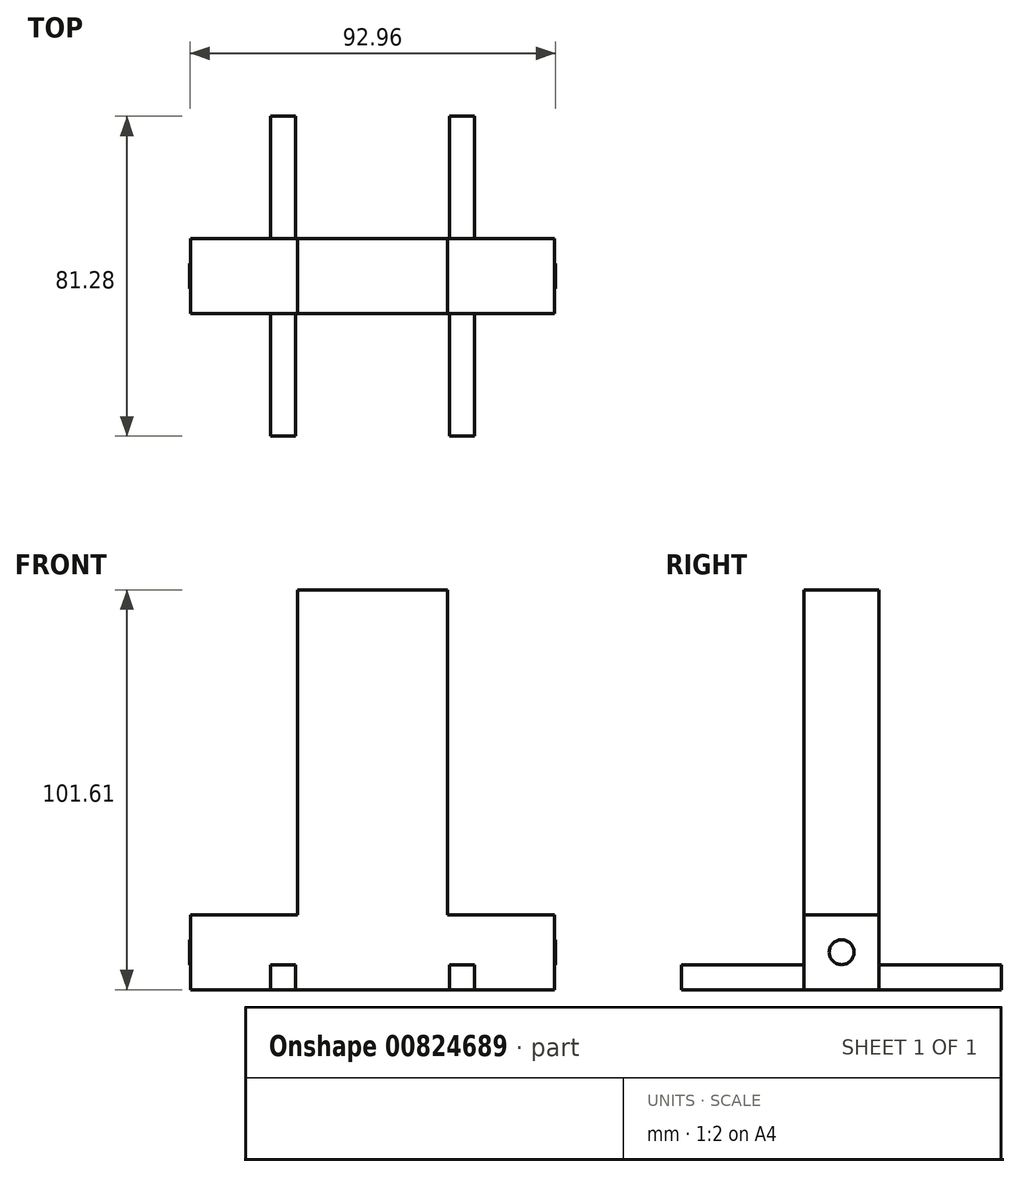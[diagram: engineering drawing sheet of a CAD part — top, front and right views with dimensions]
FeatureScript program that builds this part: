
annotation { "Feature Type Name" : "Feature", "Feature Type Description" : "" }
export const myFeature = defineFeature(function(context is Context, id is Id, definition is map)
    precondition{}
    {
        {
            var Q0;
            Q0=qCreatedBy(makeId("Right.planeOp"),FACE);
            var sketch = newSketch(context, id + "F0", { "sketchPlane" : qUnion([Q0])});
            skLineSegment(sketch, "E0.bottom", {"start": v(-9.52, 9.52) * mm, "end": v(9.53, 9.52) * mm});
            skLineSegment(sketch, "E0.top", {"start": v(-9.53, -9.53) * mm, "end": v(9.52, -9.53) * mm});
            skLineSegment(sketch, "E0.left", {"start": v(-9.52, 9.52) * mm, "end": v(-9.53, -9.53) * mm});
            skLineSegment(sketch, "E0.right", {"start": v(9.53, 9.52) * mm, "end": v(9.52, -9.53) * mm});
            skPoint(sketch, "E0.middle", {"position": v(0, 0) * mm});
            skSolve(sketch);
        }
        {
            var Q0;
            Q0=qSketchRegion(id+"F0",true);
            extrude(context, id + "F1", {"entities" : qUnion([Q0]), "endBound" : BoundingType.SYMMETRIC, "depth" : 92.46 * mm, "offsetDistance" : 25.4 * mm});
        }
        {
            var Q0;
            Q0=makeQuery(id+"F1.opExtrude","SWEPT_FACE",FACE,{"disambiguationData":[OSD([sQuery(id+"F0.wireOp",EDGE,"E0.right")])]});
            var sketch = newSketch(context, id + "F2", { "sketchPlane" : qUnion([Q0])});
            skLineSegment(sketch, "E1", {"start": v(-46.23, 9.53) * mm, "end": v(-46.23, -9.53) * mm});
            skLineSegment(sketch, "E2", {"start": v(-46.23, -9.53) * mm, "end": v(46.23, -9.53) * mm});
            skLineSegment(sketch, "E3", {"start": v(46.23, -9.53) * mm, "end": v(46.23, 9.53) * mm});
            skLineSegment(sketch, "E4", {"start": v(46.23, 9.53) * mm, "end": v(-46.23, 9.53) * mm});
            skLineSegment(sketch, "E5", {"start": v(-46.23, -9.53) * mm, "end": v(-22.73, -9.53) * mm});
            skLineSegment(sketch, "E6", {"start": v(-22.73, -9.52) * mm, "end": v(-22.73, 9.52) * mm});
            skLineSegment(sketch, "E7", {"start": v(46.23, -9.53) * mm, "end": v(22.73, -9.53) * mm});
            skLineSegment(sketch, "E8", {"start": v(22.73, -9.52) * mm, "end": v(22.73, 9.52) * mm});
            skLineSegment(sketch, "E9", {"start": v(-22.73, 0) * mm, "end": v(-46.23, 0) * mm});
            skLineSegment(sketch, "E10", {"start": v(22.73, 0) * mm, "end": v(46.23, 0) * mm});
            skLineSegment(sketch, "E11", {"start": v(-22.73, -9.53) * mm, "end": v(-19.56, -9.53) * mm});
            skLineSegment(sketch, "E12", {"start": v(-19.56, -9.53) * mm, "end": v(-19.56, -3.17) * mm});
            skLineSegment(sketch, "E13", {"start": v(-19.56, -3.17) * mm, "end": v(-25.9, -3.17) * mm});
            skLineSegment(sketch, "E14", {"start": v(-25.9, -3.18) * mm, "end": v(-25.9, -9.53) * mm});
            skLineSegment(sketch, "E15", {"start": v(-25.9, -9.53) * mm, "end": v(-19.56, -9.53) * mm});
            skLineSegment(sketch, "E16", {"start": v(22.73, -9.53) * mm, "end": v(25.9, -9.53) * mm});
            skLineSegment(sketch, "E17", {"start": v(25.9, -9.53) * mm, "end": v(25.9, -3.17) * mm});
            skLineSegment(sketch, "E18", {"start": v(25.9, -3.17) * mm, "end": v(19.56, -3.17) * mm});
            skLineSegment(sketch, "E19", {"start": v(19.56, -3.18) * mm, "end": v(19.56, -9.53) * mm});
            skLineSegment(sketch, "E20", {"start": v(19.56, -9.53) * mm, "end": v(25.9, -9.53) * mm});
            skSolve(sketch);
        }
        {
            var Q0;
            {var subQ5=sQuery(id+"F2.wireOp",EDGE,"E12");Q0=makeQuery(id+"F2.imprint","IMPRINT",FACE,{"disambiguationData":[TD([[makeQuery(id+"F2.imprint","IMPRINT",EDGE,{"derivedFrom":subQ5}),1.0]])]});}
            var Q1;
            {var subQ5=sQuery(id+"F2.wireOp",EDGE,"E14");Q1=makeQuery(id+"F2.imprint","IMPRINT",FACE,{"disambiguationData":[TD([[makeQuery(id+"F2.imprint","IMPRINT",EDGE,{"derivedFrom":subQ5}),1.0]])]});}
            var Q2;
            {var subQ5=sQuery(id+"F2.wireOp",EDGE,"E17");Q2=makeQuery(id+"F2.imprint","IMPRINT",FACE,{"disambiguationData":[TD([[makeQuery(id+"F2.imprint","IMPRINT",EDGE,{"derivedFrom":subQ5}),1.0]])]});}
            var Q3;
            {var subQ5=sQuery(id+"F2.wireOp",EDGE,"E19");Q3=makeQuery(id+"F2.imprint","IMPRINT",FACE,{"disambiguationData":[TD([[makeQuery(id+"F2.imprint","IMPRINT",EDGE,{"derivedFrom":subQ5}),1.0]])]});}
            extrude(context, id + "F3", {"entities" : qUnion([Q0, Q1, Q2, Q3]), "operationType" : NewBodyOperationType.ADD, "depth" : 31.12 * mm, "offsetDistance" : 25.4 * mm});
        }
        {
            var Q0;
            Q0=makeQuery(id+"F1.opExtrude","SWEPT_FACE",FACE,{"disambiguationData":[OSD([sQuery(id+"F0.wireOp",EDGE,"E0.left")])]});
            var sketch = newSketch(context, id + "F4", { "sketchPlane" : qUnion([Q0])});
            skLineSegment(sketch, "E21", {"start": v(-46.23, 9.52) * mm, "end": v(46.23, 9.53) * mm});
            skLineSegment(sketch, "E22", {"start": v(46.23, 9.52) * mm, "end": v(46.23, -9.53) * mm});
            skLineSegment(sketch, "E23", {"start": v(46.23, -9.53) * mm, "end": v(-46.23, -9.53) * mm});
            skLineSegment(sketch, "E24", {"start": v(-46.23, -9.53) * mm, "end": v(-46.23, 9.52) * mm});
            skLineSegment(sketch, "E25", {"start": v(-46.23, -9.53) * mm, "end": v(-22.73, -9.53) * mm});
            skLineSegment(sketch, "E26", {"start": v(-22.73, -9.53) * mm, "end": v(-22.73, 9.52) * mm});
            skLineSegment(sketch, "E27", {"start": v(46.23, -9.53) * mm, "end": v(22.73, -9.53) * mm});
            skLineSegment(sketch, "E28", {"start": v(22.73, -9.53) * mm, "end": v(22.73, 9.53) * mm});
            skLineSegment(sketch, "E29", {"start": v(-22.73, -9.53) * mm, "end": v(-19.56, -9.53) * mm});
            skLineSegment(sketch, "E30", {"start": v(-19.56, -9.53) * mm, "end": v(-19.56, -3.18) * mm});
            skLineSegment(sketch, "E31", {"start": v(-19.56, -3.18) * mm, "end": v(-25.9, -3.18) * mm});
            skLineSegment(sketch, "E32", {"start": v(-25.9, -3.18) * mm, "end": v(-25.9, -9.53) * mm});
            skLineSegment(sketch, "E33", {"start": v(-25.9, -9.53) * mm, "end": v(-19.56, -9.53) * mm});
            skLineSegment(sketch, "E34", {"start": v(22.73, -9.53) * mm, "end": v(25.9, -9.53) * mm});
            skLineSegment(sketch, "E35", {"start": v(25.9, -9.53) * mm, "end": v(25.9, -3.18) * mm});
            skLineSegment(sketch, "E36", {"start": v(25.9, -3.18) * mm, "end": v(19.56, -3.18) * mm});
            skLineSegment(sketch, "E37", {"start": v(19.56, -3.18) * mm, "end": v(19.56, -9.53) * mm});
            skLineSegment(sketch, "E38", {"start": v(19.56, -9.53) * mm, "end": v(25.9, -9.53) * mm});
            skSolve(sketch);
        }
        {
            var Q0;
            {var subQ5=sQuery(id+"F4.wireOp",EDGE,"E30");Q0=makeQuery(id+"F4.imprint","IMPRINT",FACE,{"disambiguationData":[TD([[makeQuery(id+"F4.imprint","IMPRINT",EDGE,{"derivedFrom":subQ5}),1.0]])]});}
            var Q1;
            {var subQ5=sQuery(id+"F4.wireOp",EDGE,"E32");Q1=makeQuery(id+"F4.imprint","IMPRINT",FACE,{"disambiguationData":[TD([[makeQuery(id+"F4.imprint","IMPRINT",EDGE,{"derivedFrom":subQ5}),1.0]])]});}
            var Q2;
            {var subQ5=sQuery(id+"F4.wireOp",EDGE,"E35");Q2=makeQuery(id+"F4.imprint","IMPRINT",FACE,{"disambiguationData":[TD([[makeQuery(id+"F4.imprint","IMPRINT",EDGE,{"derivedFrom":subQ5}),1.0]])]});}
            var Q3;
            {var subQ5=sQuery(id+"F4.wireOp",EDGE,"E37");Q3=makeQuery(id+"F4.imprint","IMPRINT",FACE,{"disambiguationData":[TD([[makeQuery(id+"F4.imprint","IMPRINT",EDGE,{"derivedFrom":subQ5}),1.0]])]});}
            extrude(context, id + "F5", {"entities" : qUnion([Q0, Q1, Q2, Q3]), "operationType" : NewBodyOperationType.ADD, "depth" : 31.12 * mm, "offsetDistance" : 25.4 * mm});
        }
        {
            var Q0;
            Q0=makeQuery(id+"F1.opExtrude","SWEPT_FACE",FACE,{"disambiguationData":[OSD([sQuery(id+"F0.wireOp",EDGE,"E0.bottom")])]});
            var sketch = newSketch(context, id + "F6", { "sketchPlane" : qUnion([Q0])});
            skLineSegment(sketch, "E39", {"start": v(-46.23, 9.53) * mm, "end": v(46.23, 9.53) * mm});
            skLineSegment(sketch, "E40", {"start": v(46.23, 9.53) * mm, "end": v(46.23, -9.52) * mm});
            skLineSegment(sketch, "E41", {"start": v(46.23, -9.52) * mm, "end": v(-46.23, -9.52) * mm});
            skLineSegment(sketch, "E42", {"start": v(-46.23, -9.52) * mm, "end": v(-46.23, 9.53) * mm});
            skLineSegment(sketch, "E43", {"start": v(-46.23, 9.53) * mm, "end": v(0, 9.53) * mm});
            skLineSegment(sketch, "E44", {"start": v(0, 9.53) * mm, "end": v(0, -9.52) * mm});
            skLineSegment(sketch, "E45", {"start": v(0, -9.52) * mm, "end": v(46.23, -9.52) * mm});
            skLineSegment(sketch, "E46", {"start": v(0, -9.52) * mm, "end": v(19.05, -9.52) * mm});
            skLineSegment(sketch, "E47", {"start": v(19.05, -9.52) * mm, "end": v(19.05, 9.53) * mm});
            skLineSegment(sketch, "E48", {"start": v(19.05, 9.53) * mm, "end": v(-19.05, 9.53) * mm});
            skLineSegment(sketch, "E49", {"start": v(-19.05, 9.53) * mm, "end": v(-19.05, -9.52) * mm});
            skLineSegment(sketch, "E50", {"start": v(-19.05, -9.52) * mm, "end": v(19.05, -9.52) * mm});
            skSolve(sketch);
        }
        {
            var Q0;
            {var subQ0=sQuery(id+"F6.wireOp",EDGE,"E44");Q0=makeQuery(id+"F6.imprint","IMPRINT",FACE,{"disambiguationData":[TD([[makeQuery(id+"F6.imprint","IMPRINT",EDGE,{"derivedFrom":subQ0}),1.0]])]});}
            var Q1;
            {var subQ0=sQuery(id+"F6.wireOp",EDGE,"E44");Q1=makeQuery(id+"F6.imprint","IMPRINT",FACE,{"disambiguationData":[TD([[makeQuery(id+"F6.imprint","IMPRINT",EDGE,{"derivedFrom":subQ0}),-1.0]])]});}
            extrude(context, id + "F7", {"entities" : qUnion([Q0, Q1]), "operationType" : NewBodyOperationType.ADD, "depth" : 82.55 * mm, "offsetDistance" : 25.4 * mm});
        }
        {
            var Q0;
            Q0=makeQuery(id+"F1.opExtrude","CAP_FACE",FACE,{"disambiguationData":[OSD([sQuery(id+"F0.wireOp",EDGE,"E0.bottom"),sQuery(id+"F0.wireOp",EDGE,"E0.top"),sQuery(id+"F0.wireOp",EDGE,"E0.left"),sQuery(id+"F0.wireOp",EDGE,"E0.right")])],"isStart":false});
            var sketch = newSketch(context, id + "F8", { "sketchPlane" : qUnion([Q0])});
            skCircle(sketch, "E51", {"center": v(0, 0) * mm, "radius": 3.18 * mm});
            skSolve(sketch);
        }
        {
            var Q0;
            Q0 = qSketchRegion(id + "F8", true);
            extrude(context, id + "F9", {"entities" : qUnion([Q0]), "operationType" : NewBodyOperationType.ADD, "depth" : 0.25 * mm, "offsetDistance" : 25.4 * mm});
        }
        {
            var Q0;
            Q0=makeQuery(id+"F1.opExtrude","CAP_FACE",FACE,{"disambiguationData":[OSD([sQuery(id+"F0.wireOp",EDGE,"E0.bottom"),sQuery(id+"F0.wireOp",EDGE,"E0.top"),sQuery(id+"F0.wireOp",EDGE,"E0.left"),sQuery(id+"F0.wireOp",EDGE,"E0.right")])],"isStart":true});
            var sketch = newSketch(context, id + "F10", { "sketchPlane" : qUnion([Q0])});
            skCircle(sketch, "E52", {"center": v(0, 0) * mm, "radius": 3.18 * mm});
            skSolve(sketch);
        }
        {
            var Q0;
            Q0 = qSketchRegion(id + "F10", true);
            extrude(context, id + "F11", {"entities" : qUnion([Q0]), "operationType" : NewBodyOperationType.ADD, "depth" : 0.25 * mm, "offsetDistance" : 25.4 * mm});
        }
    });
